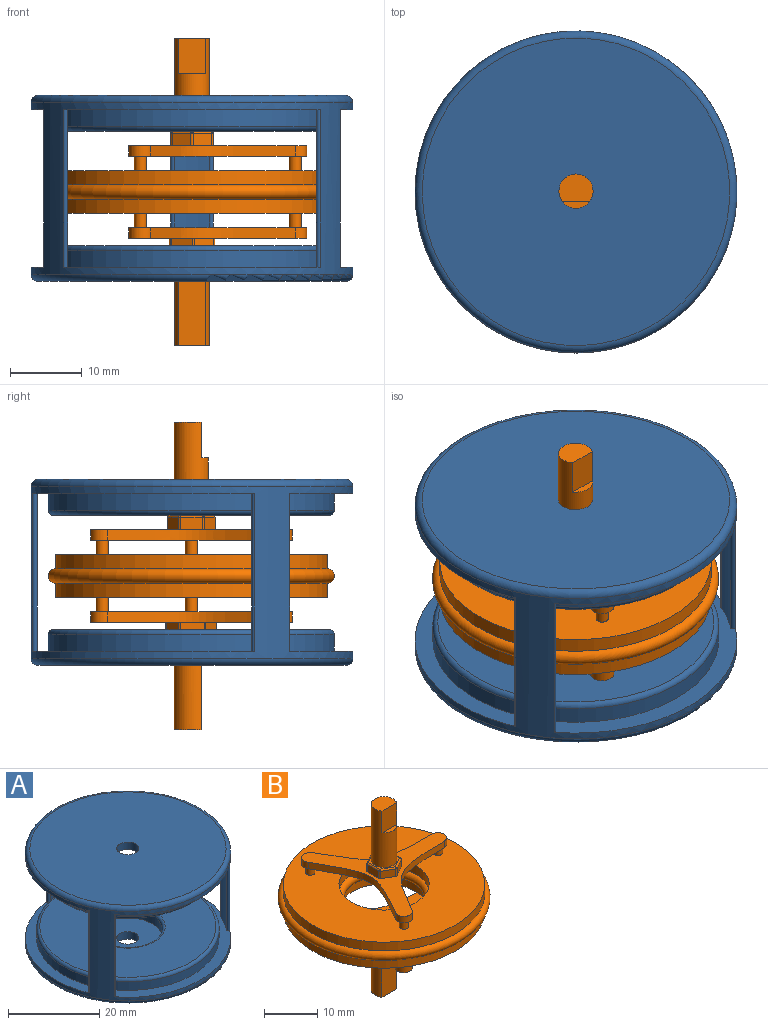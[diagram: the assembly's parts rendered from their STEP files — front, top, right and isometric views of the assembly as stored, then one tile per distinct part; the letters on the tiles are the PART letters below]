
ASSEMBLY  parts=2 mates=1
PART A: 30 faces, bbox 48.7x48.7x26 mm
  f0: plane 45x44.82mm, normal (0,0,1), area 322mm2, adj f3,f6,f10,f11,f12,f13,f14,f15
  f1: plane 15x15mm, normal (0,0,1), area 158.8mm2, adj f2,f5
  f2: cylinder r=2.39mm len=4.78mm, axis (0,0,-1), area 30mm2, adj f1,f4
  f3: cylinder r=22.5mm len=45mm, axis (0,0,-1), area 656.4mm2, adj f0,f10,f12,f13,f15,f16,f18,f19
  f4: plane 43x43mm, normal (0,0,-1), area 1434.3mm2, adj f2,f29
  f5: cylinder r=7.5mm len=15mm, axis (0,0,-1), area 108.4mm2, adj f1,f8
  f6: cylinder r=20mm len=40mm, axis (0,0,-1), area 289mm2, adj f0,f9
  f7: plane 38.6x38.6mm, normal (0,0,1), area 959mm2, adj f8,f9
  f8: torus R=8.2mm, axis (0,0,1), area 53.6mm2, adj f5,f7
  f9: torus R=19.3mm, axis (0,0,1), area 136.4mm2, adj f6,f7
  f10: cylinder r=0.37mm len=22mm, axis (0,0,-1), area 24.9mm2, adj f0,f3,f11,f19
  f11: cylinder r=21.83mm len=22mm, axis (0,0,-1), area 107.8mm2, adj f0,f10,f12,f19
  f12: cylinder r=0.37mm len=22mm, axis (0,0,-1), area 24.9mm2, adj f0,f3,f11,f19
  f13: cylinder r=0.37mm len=22mm, axis (0,0,-1), area 24.9mm2, adj f0,f3,f14,f19
  f14: cylinder r=21.83mm len=22mm, axis (0,0,-1), area 107.8mm2, adj f0,f13,f15,f19
  f15: cylinder r=0.37mm len=22mm, axis (0,0,-1), area 24.9mm2, adj f0,f3,f14,f19
  f16: cylinder r=0.37mm len=22mm, axis (0,0,-1), area 24.9mm2, adj f0,f3,f17,f19
  f17: cylinder r=21.83mm len=22mm, axis (0,0,-1), area 107.8mm2, adj f0,f16,f18,f19
  f18: cylinder r=0.37mm len=22mm, axis (0,0,-1), area 24.9mm2, adj f0,f3,f17,f19
  f19: plane 45x44.82mm, normal (0,0,-1), area 322mm2, adj f3,f10,f11,f12,f13,f14,f15,f16
  f20: plane 15x15mm, normal (0,0,-1), area 158.8mm2, adj f21,f23
  f21: cylinder r=2.39mm len=4.78mm, axis (0,0,1), area 30mm2, adj f20,f22
  f22: plane 43x43mm, normal (0,0,1), area 1434.3mm2, adj f21,f28
  f23: cylinder r=7.5mm len=15mm, axis (0,0,1), area 108.4mm2, adj f20,f26
  f24: cylinder r=20mm len=40mm, axis (0,0,1), area 289mm2, adj f19,f27
  f25: plane 38.6x38.6mm, normal (0,0,-1), area 959mm2, adj f26,f27
  f26: torus R=8.2mm, axis (0,0,-1), area 53.6mm2, adj f23,f25
  f27: torus R=19.3mm, axis (0,0,-1), area 136.4mm2, adj f24,f25
  f28: torus R=21.5mm, axis (0,0,-1), area 218.5mm2, adj f3,f22
  f29: torus R=21.5mm, axis (0,0,1), area 218.5mm2, adj f3,f4
PART B: 84 faces, bbox 43.3x43.3x43 mm
  f0: torus R=8.5mm, axis (0,0,1), area 155.2mm2, adj f3,f46
  f1: torus R=19mm, axis (0,0,1), area 387.6mm2, adj f2,f45
  f2: cylinder r=19mm len=38mm, axis (0,0,1), area 238.8mm2, adj f1,f4
  f3: cylinder r=8.5mm len=17mm, axis (0,0,1), area 106.8mm2, adj f0,f4
  f4: plane 38x38mm, normal (0,0,-1), area 900.4mm2, adj f2,f3,f41,f42,f44
  f5: plane 4.78x3.78mm, normal (0,0,-1), area 15.2mm2, adj f6,f8
  f6: plane 9x3.88mm, normal (0,-1,0), area 34.9mm2, adj f5,f7,f8
  f7: plane 3.88x1mm, normal (0,0,-1), area 2.7mm2, adj f6,f8
  f8: cylinder r=2.39mm len=13mm, axis (0,0,1), area 154.3mm2, adj f5,f6,f7,f9
  f9: plane 6.55x5.82mm, normal (0,0,-1), area 10mm2, adj f8,f11,f13,f15,f17,f19,f21
  f10: sphere r=0.3mm, area 0.1mm2, adj f11,f21,f22
  f11: cylinder r=0.3mm len=3.05mm, axis (-0.89,0.46,0), area 1.5mm2, adj f9,f10,f12,f23
  f12: sphere r=0.3mm, area 0.1mm2, adj f11,f13,f24
  f13: cylinder r=0.3mm len=3.29mm, axis (-0.04,1,0), area 1.5mm2, adj f9,f12,f14,f25
  f14: sphere r=0.3mm, area 0.1mm2, adj f13,f15,f26
  f15: cylinder r=0.3mm len=2.93mm, axis (0.84,0.54,0), area 1.5mm2, adj f9,f14,f16,f27
  f16: sphere r=0.3mm, area 0.1mm2, adj f15,f17,f28
  f17: cylinder r=0.3mm len=3.05mm, axis (0.89,-0.46,0), area 1.5mm2, adj f9,f16,f18,f29
  f18: sphere r=0.3mm, area 0.1mm2, adj f17,f19,f30
  f19: cylinder r=0.3mm len=3.29mm, axis (0.04,-1,0), area 1.5mm2, adj f9,f18,f20,f31
  f20: sphere r=0.3mm, area 0.1mm2, adj f19,f21,f32
  f21: cylinder r=0.3mm len=2.93mm, axis (-0.84,-0.54,0), area 1.5mm2, adj f9,f10,f20,f33
  f22: cylinder r=0.3mm len=1.7mm, axis (0,0,1), area 0.5mm2, adj f10,f23,f33,f34
  f23: plane 2.91x1.7mm, normal (0.46,0.89,0), area 5.6mm2, adj f11,f22,f24,f34
  f24: cylinder r=0.3mm len=1.7mm, axis (0,0,1), area 0.5mm2, adj f12,f23,f25,f34
  f25: plane 3.28x1.7mm, normal (1,0.04,0), area 5.6mm2, adj f13,f24,f26,f34
  f26: cylinder r=0.3mm len=1.7mm, axis (0,0,1), area 0.5mm2, adj f14,f25,f27,f34
  f27: plane 2.77x1.76mm, normal (0.54,-0.84,0), area 5.6mm2, adj f15,f26,f28,f34
  f28: cylinder r=0.3mm len=1.7mm, axis (0,0,1), area 0.5mm2, adj f16,f27,f29,f34
  f29: plane 2.91x1.7mm, normal (-0.46,-0.89,0), area 5.6mm2, adj f17,f28,f30,f34
  f30: cylinder r=0.3mm len=1.7mm, axis (0,0,1), area 0.5mm2, adj f18,f29,f31,f34
  f31: plane 3.28x1.7mm, normal (-1,-0.04,0), area 5.6mm2, adj f19,f30,f32,f34
  f32: cylinder r=0.3mm len=1.7mm, axis (0,0,1), area 0.5mm2, adj f20,f31,f33,f34
  f33: plane 2.77x1.76mm, normal (-0.54,0.84,0), area 5.6mm2, adj f21,f22,f32,f34
  f34: plane 28.18x24.84mm, normal (0,0,-1), area 140.6mm2, adj f22,f23,f24,f25,f26,f27,f28,f29
  f35: cylinder r=1.62mm len=3.02mm, axis (0,0,1), area 7.6mm2, adj f34,f36,f40,f43
  f36: extruded ~20.2x11.67mm, area 38.4mm2, adj f34,f35,f37,f43
  f37: cylinder r=1.62mm len=3.23mm, axis (0,0,1), area 7.6mm2, adj f34,f36,f38,f43
  f38: extruded ~20.2x11.67mm, area 38.3mm2, adj f34,f37,f39,f43
  f39: cylinder r=1.62mm len=3.02mm, axis (0,0,1), area 7.6mm2, adj f34,f38,f40,f43
  f40: extruded ~23.33x4.99mm, area 38.4mm2, adj f34,f35,f39,f43
  f41: cylinder r=0.85mm len=2mm, axis (0,0,-1), area 10.7mm2, adj f4,f43
  f42: cylinder r=0.85mm len=2mm, axis (0,0,-1), area 10.7mm2, adj f4,f43
  f43: plane 28.18x24.84mm, normal (0,0,1), area 167.9mm2, adj f35,f36,f37,f38,f39,f40,f41,f42
  f44: cylinder r=0.85mm len=2mm, axis (0,0,-1), area 10.7mm2, adj f4,f43
  f45: cylinder r=19mm len=38mm, axis (0,0,-1), area 238.8mm2, adj f1,f47
  f46: cylinder r=8.5mm len=17mm, axis (0,0,-1), area 106.8mm2, adj f0,f47
  f47: plane 38x38mm, normal (0,0,1), area 900.4mm2, adj f45,f46,f80,f81,f83
  f48: plane 4.78x3.78mm, normal (0,0,1), area 15.2mm2, adj f49,f51
  f49: plane 5x3.88mm, normal (0,-1,0), area 19.4mm2, adj f48,f50,f51
  f50: plane 3.88x1mm, normal (0,0,1), area 2.7mm2, adj f49,f51
  f51: cylinder r=2.39mm len=13mm, axis (0,0,-1), area 172.4mm2, adj f48,f49,f50,f56
  f52: sphere r=0.3mm, area 0.1mm2, adj f53,f61,f62
  f53: cylinder r=0.3mm len=2.79mm, axis (-0.87,-0.5,0), area 1.4mm2, adj f52,f54,f56,f63
  f54: sphere r=0.3mm, area 0.1mm2, adj f53,f55,f64
  f55: cylinder r=0.3mm len=3.39mm, axis (0,-1,0), area 1.5mm2, adj f54,f56,f65,f66
  f56: plane 6.27x5.28mm, normal (0,0,1), area 7.1mm2, adj f51,f53,f55,f57,f59,f61,f66
  f57: cylinder r=0.3mm len=3.09mm, axis (0.87,0.5,0), area 1.5mm2, adj f56,f58,f66,f67,f68
  f58: sphere r=0.3mm, area 0.1mm2, adj f57,f59,f69
  f59: cylinder r=0.3mm len=3.05mm, axis (0,1,0), area 1.4mm2, adj f56,f58,f60,f70
  f60: sphere r=0.3mm, area 0.1mm2, adj f59,f61,f71
  f61: cylinder r=0.3mm len=2.79mm, axis (-0.87,0.5,0), area 1.4mm2, adj f52,f56,f60,f72
  f62: cylinder r=0.3mm len=1.7mm, axis (0,0,-1), area 0.5mm2, adj f52,f63,f72,f73
  f63: plane 2.64x1.7mm, normal (0.5,-0.87,0), area 5.2mm2, adj f53,f62,f64,f73
  f64: cylinder r=0.3mm len=1.7mm, axis (0,0,-1), area 0.5mm2, adj f54,f63,f65,f73
  f65: plane 3.22x1.7mm, normal (1,0,0), area 5.5mm2, adj f55,f64,f66,f73
  f66: plane 2.79x2mm, normal (0.5,0.87,0), area 6.4mm2, adj f55,f56,f57,f65,f67,f73
  f67: cylinder r=0.3mm len=1.96mm, axis (0,0,-1), area 0.6mm2, adj f57,f66,f68,f73
  f68: plane 2.64x1.7mm, normal (-0.5,0.87,0), area 5.2mm2, adj f57,f67,f69,f73
  f69: cylinder r=0.3mm len=1.7mm, axis (0,0,-1), area 0.5mm2, adj f58,f68,f70,f73
  f70: plane 3.05x1.7mm, normal (-1,0,0), area 5.2mm2, adj f59,f69,f71,f73
  f71: cylinder r=0.3mm len=1.7mm, axis (0,0,-1), area 0.5mm2, adj f60,f70,f72,f73
  f72: plane 2.64x1.7mm, normal (-0.5,-0.87,0), area 5.2mm2, adj f61,f62,f71,f73
  f73: plane 28.18x24.84mm, normal (0,0,1), area 144.8mm2, adj f62,f63,f64,f65,f66,f67,f68,f69
  f74: cylinder r=1.62mm len=3.23mm, axis (0,0,-1), area 7.6mm2, adj f73,f75,f79,f82
  f75: extruded ~20.2x11.67mm, area 38.4mm2, adj f73,f74,f76,f82
  f76: cylinder r=1.62mm len=3.02mm, axis (0,0,-1), area 7.6mm2, adj f73,f75,f77,f82
  f77: extruded ~23.33x4.99mm, area 38.4mm2, adj f73,f76,f78,f82
  f78: cylinder r=1.62mm len=3.02mm, axis (0,0,-1), area 7.6mm2, adj f73,f77,f79,f82
  f79: extruded ~20.2x11.67mm, area 38.3mm2, adj f73,f74,f78,f82
  f80: cylinder r=0.85mm len=2mm, axis (0,0,-1), area 10.7mm2, adj f47,f82
  f81: cylinder r=0.85mm len=2mm, axis (0,0,-1), area 10.7mm2, adj f47,f82
  f82: plane 28.18x24.84mm, normal (0,0,-1), area 167.9mm2, adj f74,f75,f76,f77,f78,f79,f80,f81
  f83: cylinder r=0.85mm len=2mm, axis (0,0,-1), area 10.7mm2, adj f47,f82
PLACE A t=(1.14,0.13,-22.16)mm
PLACE B t=(1.14,0.22,-9.66)mm
MATE revolute A.f2 <-> B.f8  axis (0,0,-1) through (1.14,0.22,-22.16)mm
